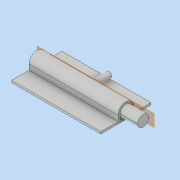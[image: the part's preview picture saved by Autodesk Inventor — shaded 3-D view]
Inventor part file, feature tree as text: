
AUTODESK INVENTOR PART (.ipt)
format: ipt  version: 2019 (Build 230136000, 136)  size: 159,744 bytes
history: native  units: mm
features: other x6, extrude x4, sketch x1, projected_geometry x1
ambient origin geometry x8: Origin, YZ Plane, XZ Plane, XY Plane, X Axis, Y Axis, Z Axis, Center Point
bodies: Body1 (feature_tree)
feature tree (12):
  other  "Твердое тело1"
  extrude  "Выдавливание1"  Depth=10.0mm
  extrude  "Выдавливание2"  Depth=80.0mm TaperAngle=0.0deg
  extrude  "Выдавливание3"  Depth=80.0mm TaperAngle=0.0deg
  sketch  "Эскиз4"
  other  "РабПлоскость2"
  extrude  "Выдавливание5"  Depth=15.61mm
  other  "Цилиндр"
  other  "Корпус"
  other  "Выемка"
  projected_geometry  "Спроецированная петля3"
  other  "Ручка"
